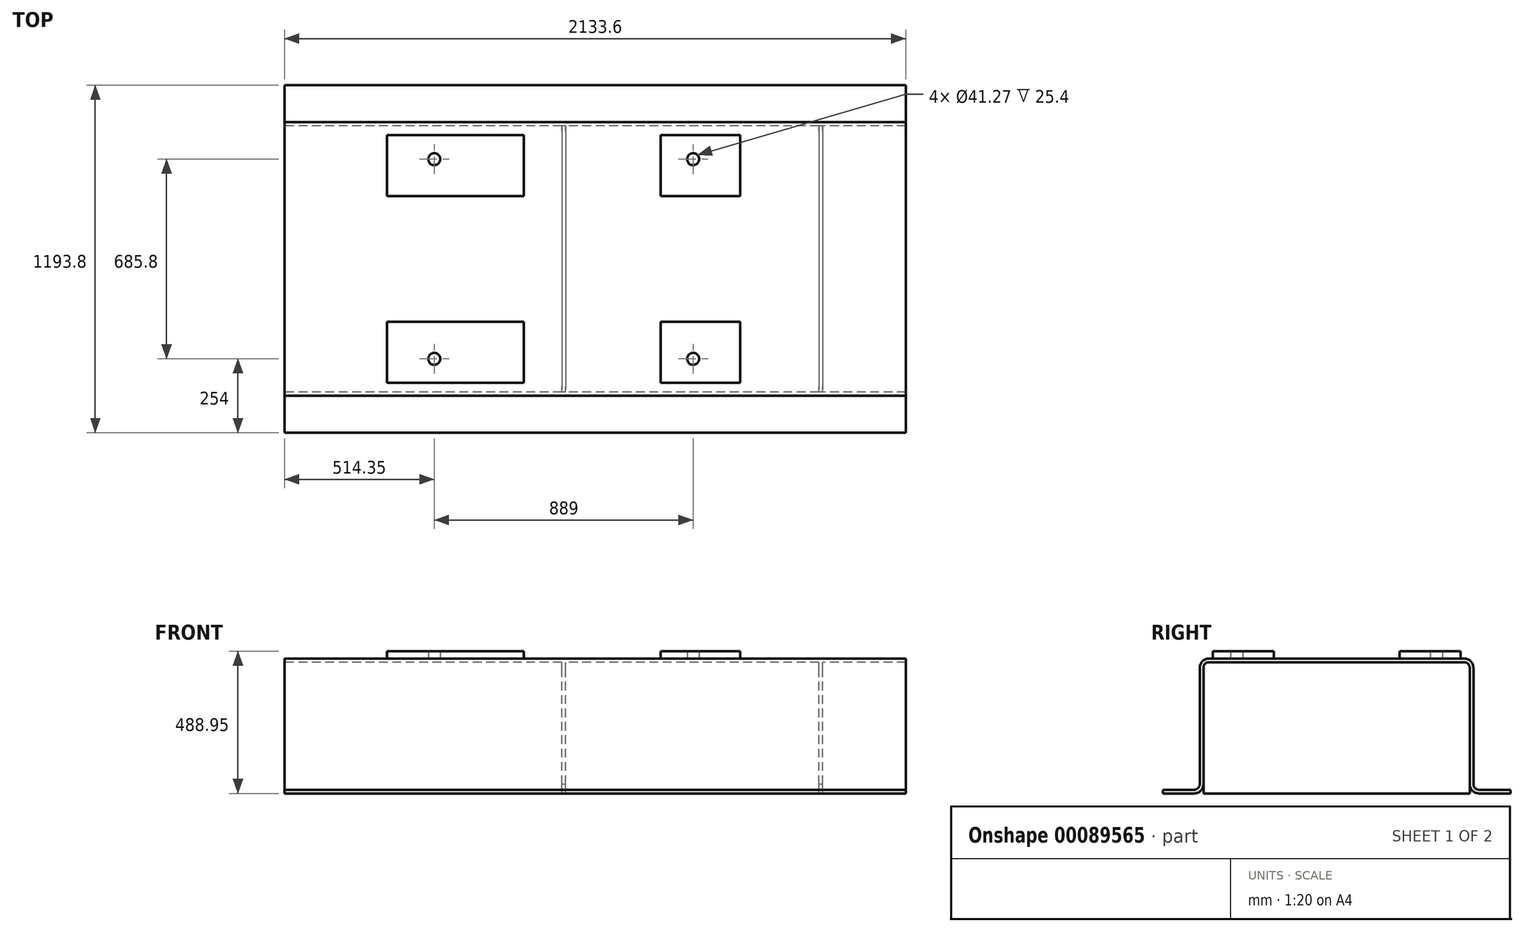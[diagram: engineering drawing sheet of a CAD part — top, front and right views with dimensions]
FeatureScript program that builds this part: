
annotation { "Feature Type Name" : "Feature", "Feature Type Description" : "" }
export const myFeature = defineFeature(function(context is Context, id is Id, definition is map)
    precondition{}
    {
        {
            var Q0;
            Q0=qCreatedBy(makeId("Right.planeOp"),FACE);
            var sketch = newSketch(context, id + "F0", { "sketchPlane" : qUnion([Q0])});
            skLineSegment(sketch, "E0", {"start": v(488.95, 0) * mm, "end": v(596.9, 0) * mm});
            skLineSegment(sketch, "E1.0", {"start": v(0, 463.55) * mm, "end": v(438.15, 463.55) * mm});
            skLineSegment(sketch, "E2", {"start": v(0, 0) * mm, "end": v(0, 543.15) * mm, "construction": true});
            skLineSegment(sketch, "E3.0", {"start": v(469.9, 31.75) * mm, "end": v(469.9, 431.8) * mm});
            skLineSegment(sketch, "E4.0", {"start": v(0, 450.85) * mm, "end": v(438.15, 450.85) * mm});
            skLineSegment(sketch, "E5.0", {"start": v(457.2, 31.75) * mm, "end": v(457.2, 431.8) * mm});
            skLineSegment(sketch, "E6.0", {"start": v(488.95, 12.7) * mm, "end": v(596.9, 12.7) * mm});
            skArc(sketch, "E7.filletArc", {"start": v(457.2, 431.8) * mm, "mid": v(451.62, 445.27) * mm, "end": v(438.15, 450.85) * mm});
            skArc(sketch, "E8.filletArc", {"start": v(469.9, 31.75) * mm, "mid": v(475.48, 18.28) * mm, "end": v(488.95, 12.7) * mm});
            skArc(sketch, "E9.filletArc", {"start": v(469.9, 431.8) * mm, "mid": v(460.6, 454.25) * mm, "end": v(438.15, 463.55) * mm});
            skPoint(sketch, "E10.newPointB", {"position": v(-596.9, 0) * mm});
            skArc(sketch, "E10.filletArc", {"start": v(457.2, 31.75) * mm, "mid": v(466.5, 9.3) * mm, "end": v(488.95, 0) * mm});
            skLineSegment(sketch, "E11", {"start": v(596.9, 12.7) * mm, "end": v(596.9, 0) * mm});
            skArc(sketch, "E12.MirrorCS", {"start": v(-469.9, 31.75) * mm, "mid": v(-475.48, 18.28) * mm, "end": v(-488.95, 12.7) * mm});
            skLineSegment(sketch, "E13.MirrorCS", {"start": v(-596.9, 12.7) * mm, "end": v(-596.9, 0) * mm});
            skArc(sketch, "E14.MirrorCS", {"start": v(-457.2, 31.75) * mm, "mid": v(-466.5, 9.3) * mm, "end": v(-488.95, 0) * mm});
            skArc(sketch, "E15.MirrorCS", {"start": v(-457.2, 431.8) * mm, "mid": v(-451.62, 445.27) * mm, "end": v(-438.15, 450.85) * mm});
            skLineSegment(sketch, "E16.MirrorCS", {"start": v(-488.95, 0) * mm, "end": v(-596.9, 0) * mm});
            skArc(sketch, "E17.MirrorCS", {"start": v(-469.9, 431.8) * mm, "mid": v(-460.6, 454.25) * mm, "end": v(-438.15, 463.55) * mm});
            skLineSegment(sketch, "E18.MirrorCS", {"start": v(-488.95, 12.7) * mm, "end": v(-596.9, 12.7) * mm});
            skLineSegment(sketch, "E19.MirrorCS", {"start": v(0, 463.55) * mm, "end": v(-438.15, 463.55) * mm});
            skLineSegment(sketch, "E20.MirrorCS", {"start": v(-469.9, 31.75) * mm, "end": v(-469.9, 431.8) * mm});
            skLineSegment(sketch, "E21.MirrorCS", {"start": v(0, 450.85) * mm, "end": v(-438.15, 450.85) * mm});
            skLineSegment(sketch, "E22.MirrorCS", {"start": v(-457.2, 31.75) * mm, "end": v(-457.2, 431.8) * mm});
            skSolve(sketch);
        }
        {
            var Q0;
            Q0=makeQuery(id+"F0.imprint","IMPRINT",FACE,{"disambiguationData":[TD([[makeQuery(id+"F0.imprint","IMPRINT",EDGE,{"derivedFrom":sQuery(id+"F0.wireOp",EDGE,"E0")}),1.0]])]});
            extrude(context, id + "F1", {"entities" : qUnion([Q0]), "endBound" : BoundingType.SYMMETRIC, "depth" : 2133.6 * mm});
        }
        {
            var Q0;
            Q0=makeQuery(id+"F1.opExtrude","SWEPT_FACE",FACE,{"disambiguationData":[OSD([sQuery(id+"F0.wireOp",EDGE,"E4.0"),sQuery(id+"F0.wireOp",EDGE,"E21.MirrorCS")])]});
            var sketch = newSketch(context, id + "F2", { "sketchPlane" : qUnion([Q0])});
            skLineSegment(sketch, "E23.0", {"start": v(1066.8, -438.15) * mm, "end": v(1066.8, 438.15) * mm, "construction": true});
            skLineSegment(sketch, "E24.0", {"start": v(-2108.2, -1491.5) * mm, "end": v(-2108.2, -509.42) * mm, "construction": true});
            skLineSegment(sketch, "E25.0", {"start": v(-1524, -1491.5) * mm, "end": v(-1524, -509.42) * mm, "construction": true});
            skLineSegment(sketch, "E26.0", {"start": v(-107.95, -1491.5) * mm, "end": v(-107.95, -457.2) * mm, "construction": true});
            skLineSegment(sketch, "E27.0", {"start": v(774.7, -1491.5) * mm, "end": v(774.7, -457.2) * mm, "construction": true});
            skLineSegment(sketch, "E28.0", {"start": v(1066.8, 457.2) * mm, "end": v(-1066.8, 457.2) * mm, "construction": true});
            skLineSegment(sketch, "E29.0", {"start": v(1066.8, -457.2) * mm, "end": v(-1066.8, -457.2) * mm, "construction": true});
            skLineSegment(sketch, "E30.bottom", {"start": v(-114.3, -457.2) * mm, "end": v(-101.6, -457.2) * mm});
            skLineSegment(sketch, "E30.top", {"start": v(-114.3, 457.2) * mm, "end": v(-101.6, 457.2) * mm});
            skLineSegment(sketch, "E30.left", {"start": v(-114.3, -457.2) * mm, "end": v(-114.3, 457.2) * mm});
            skLineSegment(sketch, "E30.right", {"start": v(-101.6, -457.2) * mm, "end": v(-101.6, 457.2) * mm});
            skLineSegment(sketch, "E31.bottom", {"start": v(768.35, -457.2) * mm, "end": v(781.05, -457.2) * mm});
            skLineSegment(sketch, "E31.top", {"start": v(768.35, 457.2) * mm, "end": v(781.05, 457.2) * mm});
            skLineSegment(sketch, "E31.left", {"start": v(768.35, -457.2) * mm, "end": v(768.35, 457.2) * mm});
            skLineSegment(sketch, "E31.right", {"start": v(781.05, -457.2) * mm, "end": v(781.05, 457.2) * mm});
            skSolve(sketch);
        }
        {
            var Q0;
            Q0 = qSketchRegion(id + "F2", true);
            var Q1;
            Q1=makeQuery(id+"F1.opExtrude","SWEPT_FACE",FACE,{"disambiguationData":[OSD([sQuery(id+"F0.wireOp",EDGE,"E16.MirrorCS")])]});
            extrude(context, id + "F3", {"entities" : qUnion([Q0]), "operationType" : NewBodyOperationType.ADD, "endBound" : BoundingType.UP_TO_SURFACE, "endBoundEntityFace" : qUnion([Q1]), "depth" : 25.4 * mm});
        }
        {
            var Q0;
            Q0=makeQuery(id+"F1.opExtrude","SWEPT_FACE",FACE,{"disambiguationData":[OSD([sQuery(id+"F0.wireOp",EDGE,"E1.0"),sQuery(id+"F0.wireOp",EDGE,"E19.MirrorCS")])]});
            var sketch = newSketch(context, id + "F4", { "sketchPlane" : qUnion([Q0])});
            skLineSegment(sketch, "E32.0", {"start": v(-107.95, 1491.5) * mm, "end": v(-107.95, 0) * mm, "construction": true});
            skLineSegment(sketch, "E33.0", {"start": v(774.7, 1491.5) * mm, "end": v(774.7, 0) * mm, "construction": true});
            skLineSegment(sketch, "E34", {"start": v(-1066.8, 0) * mm, "end": v(1224.5, 0) * mm, "construction": true});
            skPoint(sketch, "E35.orphan", {"position": v(-107.95, 457.2) * mm});
            skPoint(sketch, "E36.orphan", {"position": v(774.7, 457.2) * mm});
            skLineSegment(sketch, "E37.0", {"start": v(-244.6, 1491.5) * mm, "end": v(-244.6, 0) * mm, "construction": true});
            skLineSegment(sketch, "E38.0", {"start": v(-714.5, 1491.5) * mm, "end": v(-714.5, 0) * mm, "construction": true});
            skLineSegment(sketch, "E39.0", {"start": v(225.3, 1491.5) * mm, "end": v(225.3, 0) * mm, "construction": true});
            skLineSegment(sketch, "E40.0", {"start": v(498.35, 1491.5) * mm, "end": v(498.35, 0) * mm, "construction": true});
            skLineSegment(sketch, "E41.0", {"start": v(-1066.8, 215.9) * mm, "end": v(1224.5, 215.9) * mm, "construction": true});
            skLineSegment(sketch, "E42.0", {"start": v(-1060.45, 431.8) * mm, "end": v(-1060.45, -431.8) * mm, "construction": true});
            skLineSegment(sketch, "E42.1", {"start": v(1060.45, 431.8) * mm, "end": v(-1060.45, 431.8) * mm, "construction": true});
            skLineSegment(sketch, "E42.2", {"start": v(1060.45, -431.8) * mm, "end": v(1060.45, 431.8) * mm, "construction": true});
            skLineSegment(sketch, "E42.3", {"start": v(-1060.45, -431.8) * mm, "end": v(1060.45, -431.8) * mm, "construction": true});
            skLineSegment(sketch, "E43.0", {"start": v(-1066.8, 425.45) * mm, "end": v(1224.5, 425.45) * mm, "construction": true});
            skLineSegment(sketch, "E44.0", {"start": v(1060.45, 438.15) * mm, "end": v(-1060.45, 438.15) * mm, "construction": true});
            skLineSegment(sketch, "E45.bottom", {"start": v(-714.5, 425.45) * mm, "end": v(-244.6, 425.45) * mm});
            skLineSegment(sketch, "E45.top", {"start": v(-714.5, 215.9) * mm, "end": v(-244.6, 215.9) * mm});
            skLineSegment(sketch, "E45.left", {"start": v(-714.5, 425.45) * mm, "end": v(-714.5, 215.9) * mm});
            skLineSegment(sketch, "E45.right", {"start": v(-244.6, 425.45) * mm, "end": v(-244.6, 215.9) * mm});
            skLineSegment(sketch, "E46.bottom", {"start": v(225.3, 425.45) * mm, "end": v(498.35, 425.45) * mm});
            skLineSegment(sketch, "E46.top", {"start": v(225.3, 215.9) * mm, "end": v(498.35, 215.9) * mm});
            skLineSegment(sketch, "E46.left", {"start": v(225.3, 425.45) * mm, "end": v(225.3, 215.9) * mm});
            skLineSegment(sketch, "E46.right", {"start": v(498.35, 425.45) * mm, "end": v(498.35, 215.9) * mm});
            skLineSegment(sketch, "E47.0", {"start": v(-1066.8, 342.9) * mm, "end": v(1224.5, 342.9) * mm, "construction": true});
            skLineSegment(sketch, "E48.0", {"start": v(-552.45, 1491.5) * mm, "end": v(-552.45, 0) * mm, "construction": true});
            skLineSegment(sketch, "E49.0", {"start": v(336.55, 1491.5) * mm, "end": v(336.55, 0) * mm, "construction": true});
            skCircle(sketch, "E50", {"center": v(-552.45, 342.9) * mm, "radius": 20.64 * mm});
            skCircle(sketch, "E51", {"center": v(336.55, 342.9) * mm, "radius": 20.64 * mm});
            skCircle(sketch, "E52.MirrorC", {"center": v(-552.45, -342.9) * mm, "radius": 20.64 * mm});
            skLineSegment(sketch, "E53.MirrorCS", {"start": v(225.3, -425.45) * mm, "end": v(498.35, -425.45) * mm});
            skCircle(sketch, "E54.MirrorC", {"center": v(336.55, -342.9) * mm, "radius": 20.64 * mm});
            skPoint(sketch, "E55.MirrorP", {"position": v(-107.95, -457.2) * mm});
            skLineSegment(sketch, "E56.MirrorCS", {"start": v(-714.5, -425.45) * mm, "end": v(-714.5, -215.9) * mm});
            skLineSegment(sketch, "E57.MirrorCS", {"start": v(225.3, -425.45) * mm, "end": v(225.3, -215.9) * mm});
            skLineSegment(sketch, "E58.MirrorCS", {"start": v(-244.6, -425.45) * mm, "end": v(-244.6, -215.9) * mm});
            skLineSegment(sketch, "E59.MirrorCS", {"start": v(225.3, -215.9) * mm, "end": v(498.35, -215.9) * mm});
            skLineSegment(sketch, "E60.MirrorCS", {"start": v(-714.5, -425.45) * mm, "end": v(-244.6, -425.45) * mm});
            skLineSegment(sketch, "E61.MirrorCS", {"start": v(498.35, -425.45) * mm, "end": v(498.35, -215.9) * mm});
            skLineSegment(sketch, "E62.MirrorCS", {"start": v(-714.5, -215.9) * mm, "end": v(-244.6, -215.9) * mm});
            skSolve(sketch);
        }
        {
            var Q0;
            Q0 = qSketchRegion(id + "F4", true);
            extrude(context, id + "F5", {"entities" : qUnion([Q0]), "operationType" : NewBodyOperationType.ADD, "depth" : 25.4 * mm});
        }
    });
